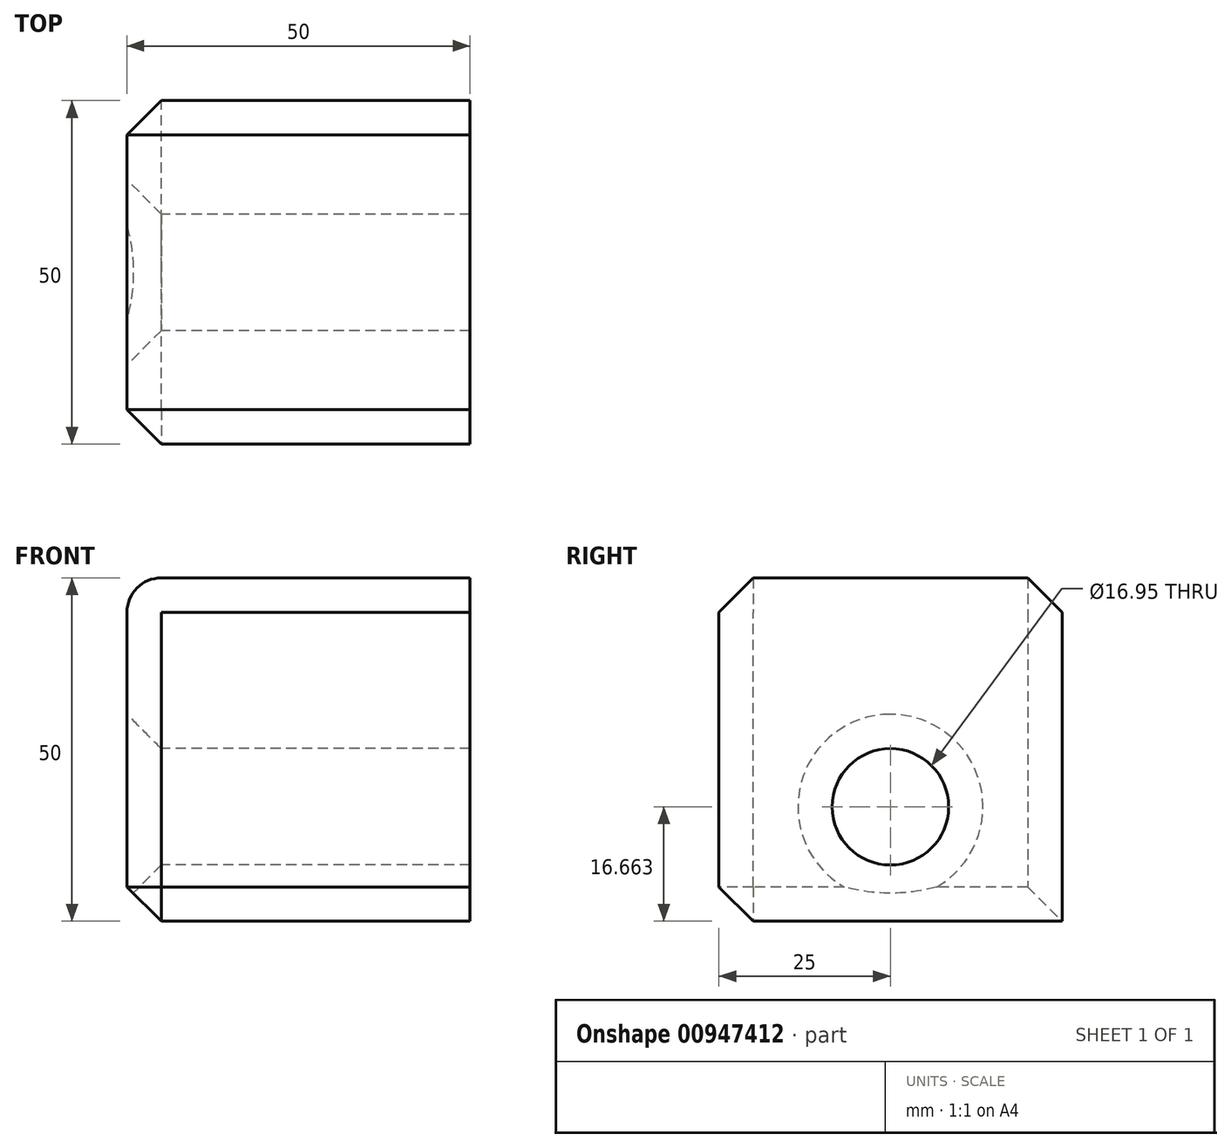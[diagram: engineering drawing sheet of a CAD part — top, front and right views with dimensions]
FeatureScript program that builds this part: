
annotation { "Feature Type Name" : "Feature", "Feature Type Description" : "" }
export const myFeature = defineFeature(function(context is Context, id is Id, definition is map)
    precondition{}
    {
        {
            var Q0;
            Q0=qCreatedBy(makeId("Top.planeOp"),FACE);
            var sketch = newSketch(context, id + "F0", { "sketchPlane" : qUnion([Q0])});
            skLineSegment(sketch, "E0.bottom", {"start": v(25, -25) * mm, "end": v(-25, -25) * mm});
            skLineSegment(sketch, "E0.top", {"start": v(25, 25) * mm, "end": v(-25, 25) * mm});
            skLineSegment(sketch, "E0.left", {"start": v(25, -25) * mm, "end": v(25, 25) * mm});
            skLineSegment(sketch, "E0.right", {"start": v(-25, -25) * mm, "end": v(-25, 25) * mm});
            skPoint(sketch, "E0.middle", {"position": v(0, 0) * mm});
            skSolve(sketch);
        }
        {
            var Q0;
            Q0=makeQuery(id+"F0.imprint","IMPRINT",FACE,{"disambiguationData":[TD([[makeQuery(id+"F0.imprint","IMPRINT",EDGE,{"derivedFrom":sQuery(id+"F0.wireOp",EDGE,"E0.bottom")}),-1.0]])]});
            extrude(context, id + "F1", {"entities" : qUnion([Q0]), "depth" : 50 * mm, "offsetDistance" : 25 * mm});
        }
        {
            var Q0;
            Q0=makeQuery(id+"F1.opExtrude","SWEPT_FACE",FACE,{"disambiguationData":[OSD([sQuery(id+"F0.wireOp",EDGE,"E0.right")])]});
            var sketch = newSketch(context, id + "F2", { "sketchPlane" : qUnion([Q0])});
            skCircle(sketch, "E1", {"center": v(0, 16.66) * mm, "radius": 8.48 * mm});
            skSolve(sketch);
        }
        {
            var Q0;
            Q0=makeQuery(id+"F2.imprint","IMPRINT",FACE,{"disambiguationData":[TD([[makeQuery(id+"F2.imprint","IMPRINT",EDGE,{"derivedFrom":sQuery(id+"F2.wireOp",EDGE,"E1")}),1.0]])]});
            extrude(context, id + "F3", {"entities" : qUnion([Q0]), "operationType" : NewBodyOperationType.REMOVE, "endBound" : BoundingType.UP_TO_NEXT, "oppositeDirection" : true, "depth" : 25 * mm, "offsetDistance" : 25 * mm});
        }
        {
            var Q0;
            Q0=makeQuery(id+"F1.opExtrude","CAP_EDGE",EDGE,{"disambiguationData":[OSD([sQuery(id+"F0.wireOp",EDGE,"E0.right")])],"isStart":false});
            fillet(context, id + "F4", {"entities" : qUnion([Q0]), "radius" : 5 * mm, "tangentPropagation" : true, "allowEdgeOverflow" : false});
        }
        {
            var Q0;
            Q0=makeQuery(id+"F1.opExtrude","CAP_EDGE",EDGE,{"disambiguationData":[OSD([sQuery(id+"F0.wireOp",EDGE,"E0.bottom")])],"isStart":false});
            var Q1;
            Q1=makeQuery(id+"F1.opExtrude","CAP_EDGE",EDGE,{"disambiguationData":[OSD([sQuery(id+"F0.wireOp",EDGE,"E0.bottom")])],"isStart":true});
            var Q2;
            Q2=makeQuery(id+"F1.opExtrude","SWEPT_FACE",FACE,{"disambiguationData":[OSD([sQuery(id+"F0.wireOp",EDGE,"E0.right")])]});
            var Q3;
            Q3=makeQuery(id+"F3.boolean.opBoolean","COPY",EDGE,{"derivedFrom":makeQuery(id+"F3.opExtrude","CAP_EDGE",EDGE,{"disambiguationData":[OSD([sQuery(id+"F2.wireOp",EDGE,"E1")])],"isStart":true})});
            chamfer(context, id + "F5", {"entities" : qUnion([Q0, Q1, Q2, Q3]), "width" : 5 * mm, "tangentPropagation" : true});
        }
    });
